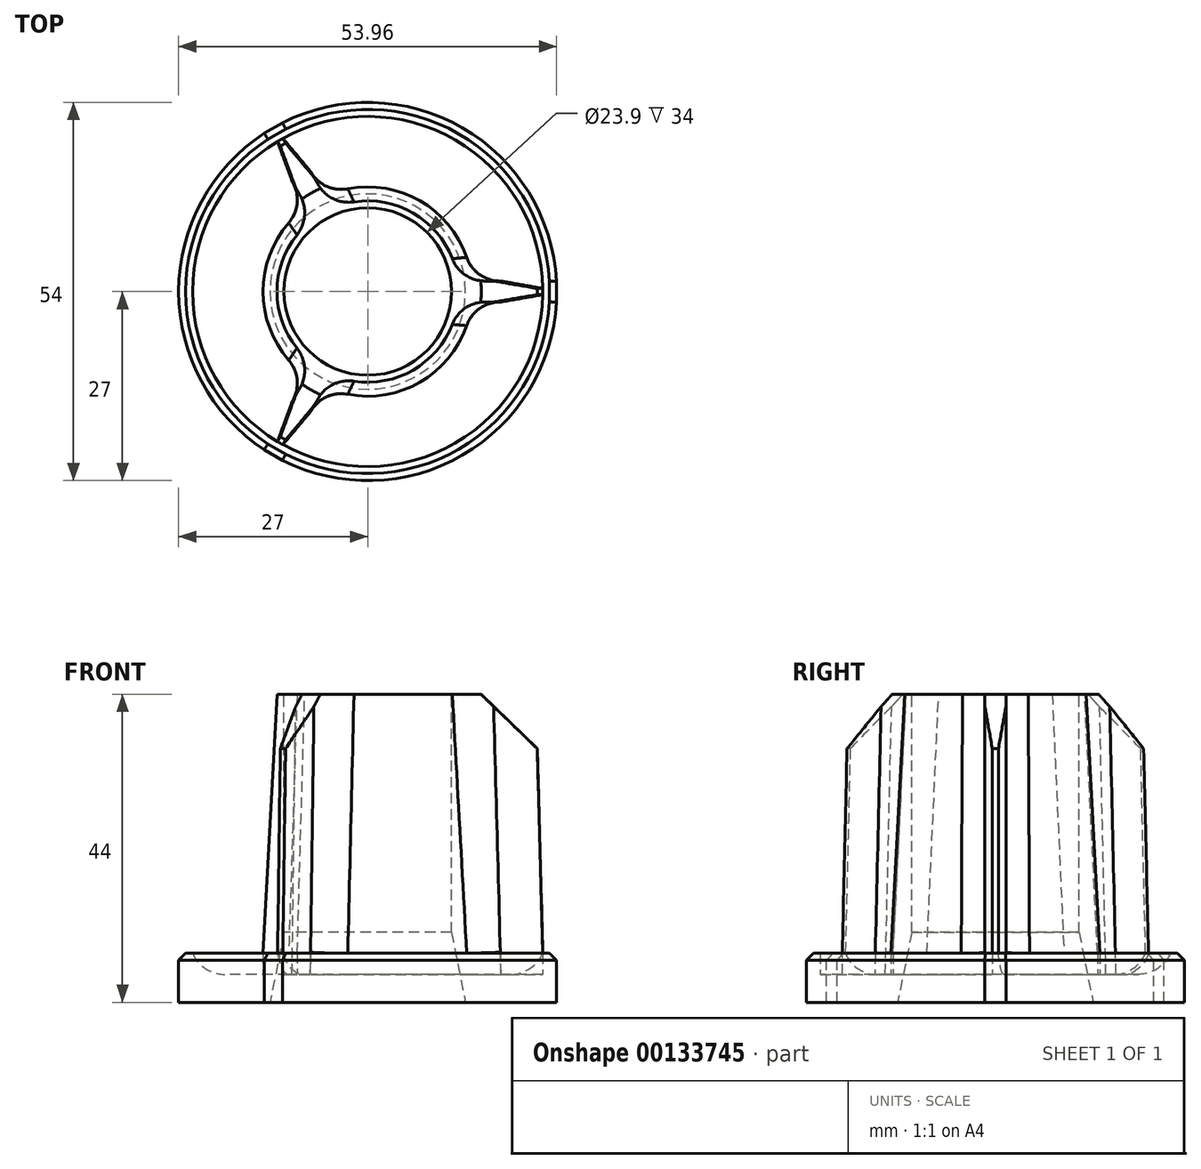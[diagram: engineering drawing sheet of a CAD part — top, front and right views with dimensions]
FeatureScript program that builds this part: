
annotation { "Feature Type Name" : "Feature", "Feature Type Description" : "" }
export const myFeature = defineFeature(function(context is Context, id is Id, definition is map)
    precondition{}
    {
        {
            var Q0;
            Q0=qCreatedBy(makeId("Top.planeOp"),FACE);
            var sketch = newSketch(context, id + "F0", { "sketchPlane" : qUnion([Q0])});
            skCircle(sketch, "E0", {"center": v(0, 0) * mm, "radius": 27 * mm});
            skCircle(sketch, "E1", {"center": v(0, 0) * mm, "radius": 11.95 * mm});
            skLineSegment(sketch, "E2", {"start": v(14.87, 1.5) * mm, "end": v(26.96, 1.5) * mm});
            skLineSegment(sketch, "E3", {"start": v(14.87, -1.5) * mm, "end": v(26.96, -1.5) * mm});
            skLineSegment(sketch, "E4", {"start": v(26.96, -1.5) * mm, "end": v(26.96, 1.5) * mm});
            skLineSegment(sketch, "E5.1.0", {"start": v(-6.14, 13.63) * mm, "end": v(-12.18, 24.1) * mm});
            skLineSegment(sketch, "E5.1.1", {"start": v(-12.18, 24.1) * mm, "end": v(-14.78, 22.6) * mm});
            skLineSegment(sketch, "E5.1.2", {"start": v(-8.74, 12.13) * mm, "end": v(-14.78, 22.6) * mm});
            skLineSegment(sketch, "E5.2.0", {"start": v(-8.74, -12.13) * mm, "end": v(-14.78, -22.6) * mm});
            skLineSegment(sketch, "E5.2.1", {"start": v(-14.78, -22.6) * mm, "end": v(-12.18, -24.1) * mm});
            skLineSegment(sketch, "E5.2.2", {"start": v(-6.14, -13.63) * mm, "end": v(-12.18, -24.1) * mm});
            skCircle(sketch, "E6", {"center": v(0, 0) * mm, "radius": 14.95 * mm, "construction": true});
            skArc(sketch, "E7", {"start": v(14.87, 1.5) * mm, "mid": v(7.47, 12.95) * mm, "end": v(-6.14, 13.63) * mm});
            skArc(sketch, "E8", {"start": v(-8.74, 12.13) * mm, "mid": v(-14.95, 0) * mm, "end": v(-8.74, -12.13) * mm});
            skArc(sketch, "E9", {"start": v(-6.14, -13.63) * mm, "mid": v(7.48, -12.95) * mm, "end": v(14.87, -1.5) * mm});
            skCircle(sketch, "E10", {"center": v(0, 0) * mm, "radius": 25 * mm});
            skSolve(sketch);
        }
        {
            var Q0;
            {var subQ0=sQuery(id+"F0.wireOp",EDGE,"E7");Q0=makeQuery(id+"F0.imprint","IMPRINT",FACE,{"disambiguationData":[TD([[makeQuery(id+"F0.imprint","IMPRINT",EDGE,{"derivedFrom":subQ0}),-1.0]])]});}
            var Q1;
            {var subQ0=sQuery(id+"F0.wireOp",EDGE,"E2");var subQ5=sQuery(id+"F0.wireOp",EDGE,"E10");var subQ6=makeQuery(id+"F0.imprint","INTERSECT",VERTEX,{"derivedFrom":[subQ0,subQ5]});Q1=makeQuery(id+"F0.imprint","IMPRINT",FACE,{"disambiguationData":[TD([[makeQuery(id+"F0.imprint","IMPRINT",EDGE,{"disambiguationData":[TD([[subQ6,-1.0]])],"derivedFrom":subQ5}),-1.0]])]});}
            var Q2;
            {var subQ0=sQuery(id+"F0.wireOp",EDGE,"E5.1.1");Q2=makeQuery(id+"F0.imprint","IMPRINT",FACE,{"disambiguationData":[TD([[makeQuery(id+"F0.imprint","IMPRINT",EDGE,{"derivedFrom":subQ0}),1.0]])]});}
            var Q3;
            {var subQ0=sQuery(id+"F0.wireOp",EDGE,"E5.1.2");var subQ5=sQuery(id+"F0.wireOp",EDGE,"E10");var subQ6=makeQuery(id+"F0.imprint","INTERSECT",VERTEX,{"derivedFrom":[subQ0,subQ5]});Q3=makeQuery(id+"F0.imprint","IMPRINT",FACE,{"disambiguationData":[TD([[makeQuery(id+"F0.imprint","IMPRINT",EDGE,{"disambiguationData":[TD([[subQ6,-1.0]])],"derivedFrom":subQ5}),-1.0]])]});}
            var Q4;
            {var subQ0=sQuery(id+"F0.wireOp",EDGE,"E9");Q4=makeQuery(id+"F0.imprint","IMPRINT",FACE,{"disambiguationData":[TD([[makeQuery(id+"F0.imprint","IMPRINT",EDGE,{"derivedFrom":subQ0}),-1.0]])]});}
            var Q5;
            {var subQ0=sQuery(id+"F0.wireOp",EDGE,"E3");var subQ5=sQuery(id+"F0.wireOp",EDGE,"E10");var subQ7=makeQuery(id+"F0.imprint","INTERSECT",VERTEX,{"derivedFrom":[subQ0,subQ5]});Q5=makeQuery(id+"F0.imprint","IMPRINT",FACE,{"disambiguationData":[TD([[makeQuery(id+"F0.imprint","IMPRINT",EDGE,{"disambiguationData":[TD([[subQ7,1.0]])],"derivedFrom":subQ5}),-1.0]])]});}
            var Q6;
            Q6=makeQuery(id+"F0.imprint","IMPRINT",FACE,{"disambiguationData":[TD([[makeQuery(id+"F0.imprint","IMPRINT",EDGE,{"derivedFrom":sQuery(id+"F0.wireOp",EDGE,"E1")}),-1.0]])]});
            var Q7;
            {var subQ0=sQuery(id+"F0.wireOp",EDGE,"E5.2.1");Q7=makeQuery(id+"F0.imprint","IMPRINT",FACE,{"disambiguationData":[TD([[makeQuery(id+"F0.imprint","IMPRINT",EDGE,{"derivedFrom":subQ0}),1.0]])]});}
            var Q8;
            {var subQ0=sQuery(id+"F0.wireOp",EDGE,"E4");Q8=makeQuery(id+"F0.imprint","IMPRINT",FACE,{"disambiguationData":[TD([[makeQuery(id+"F0.imprint","IMPRINT",EDGE,{"derivedFrom":subQ0}),1.0]])]});}
            var Q9;
            {var subQ0=sQuery(id+"F0.wireOp",EDGE,"E8");Q9=makeQuery(id+"F0.imprint","IMPRINT",FACE,{"disambiguationData":[TD([[makeQuery(id+"F0.imprint","IMPRINT",EDGE,{"derivedFrom":subQ0}),-1.0]])]});}
            extrude(context, id + "F1", {"entities" : qUnion([Q0, Q1, Q2, Q3, Q4, Q5, Q6, Q7, Q8, Q9]), "oppositeDirection" : true, "depth" : 4 * mm});
        }
        {
            var Q0;
            Q0=makeQuery(id+"F0.imprint","IMPRINT",FACE,{"disambiguationData":[TD([[makeQuery(id+"F0.imprint","IMPRINT",EDGE,{"derivedFrom":sQuery(id+"F0.wireOp",EDGE,"E1")}),-1.0]])]});
            extrude(context, id + "F2", {"entities" : qUnion([Q0]), "operationType" : NewBodyOperationType.ADD, "depth" : 40 * mm});
        }
        {
            var Q0;
            {var subQ0=sQuery(id+"F0.wireOp",EDGE,"E5.1.2");var subQ5=sQuery(id+"F0.wireOp",EDGE,"E10");var subQ6=makeQuery(id+"F0.imprint","INTERSECT",VERTEX,{"derivedFrom":[subQ0,subQ5]});Q0=makeQuery(id+"F0.imprint","IMPRINT",FACE,{"disambiguationData":[TD([[makeQuery(id+"F0.imprint","IMPRINT",EDGE,{"disambiguationData":[TD([[subQ6,-1.0]])],"derivedFrom":subQ5}),-1.0]])]});}
            var Q1;
            {var subQ0=sQuery(id+"F0.wireOp",EDGE,"E3");var subQ5=sQuery(id+"F0.wireOp",EDGE,"E10");var subQ7=makeQuery(id+"F0.imprint","INTERSECT",VERTEX,{"derivedFrom":[subQ0,subQ5]});Q1=makeQuery(id+"F0.imprint","IMPRINT",FACE,{"disambiguationData":[TD([[makeQuery(id+"F0.imprint","IMPRINT",EDGE,{"disambiguationData":[TD([[subQ7,1.0]])],"derivedFrom":subQ5}),-1.0]])]});}
            var Q2;
            {var subQ0=sQuery(id+"F0.wireOp",EDGE,"E5.2.1");Q2=makeQuery(id+"F0.imprint","IMPRINT",FACE,{"disambiguationData":[TD([[makeQuery(id+"F0.imprint","IMPRINT",EDGE,{"derivedFrom":subQ0}),1.0]])]});}
            var Q3;
            {var subQ0=sQuery(id+"F0.wireOp",EDGE,"E4");Q3=makeQuery(id+"F0.imprint","IMPRINT",FACE,{"disambiguationData":[TD([[makeQuery(id+"F0.imprint","IMPRINT",EDGE,{"derivedFrom":subQ0}),1.0]])]});}
            var Q4;
            {var subQ0=sQuery(id+"F0.wireOp",EDGE,"E2");var subQ5=sQuery(id+"F0.wireOp",EDGE,"E10");var subQ6=makeQuery(id+"F0.imprint","INTERSECT",VERTEX,{"derivedFrom":[subQ0,subQ5]});Q4=makeQuery(id+"F0.imprint","IMPRINT",FACE,{"disambiguationData":[TD([[makeQuery(id+"F0.imprint","IMPRINT",EDGE,{"disambiguationData":[TD([[subQ6,-1.0]])],"derivedFrom":subQ5}),-1.0]])]});}
            var Q5;
            {var subQ0=sQuery(id+"F0.wireOp",EDGE,"E5.1.1");Q5=makeQuery(id+"F0.imprint","IMPRINT",FACE,{"disambiguationData":[TD([[makeQuery(id+"F0.imprint","IMPRINT",EDGE,{"derivedFrom":subQ0}),1.0]])]});}
            extrude(context, id + "F3", {"entities" : qUnion([Q0, Q1, Q2, Q3, Q4, Q5]), "operationType" : NewBodyOperationType.ADD, "depth" : 3 * mm});
        }
        {
            var Q0;
            Q0=makeQuery(id+"F2.opExtrude","CAP_EDGE",EDGE,{"disambiguationData":[OSD([sQuery(id+"F0.wireOp",EDGE,"E7")])],"isStart":false});
            var Q1;
            Q1=makeQuery(id+"F2.opExtrude","CAP_EDGE",EDGE,{"disambiguationData":[OSD([sQuery(id+"F0.wireOp",EDGE,"E8")])],"isStart":false});
            var Q2;
            Q2=makeQuery(id+"F2.opExtrude","CAP_EDGE",EDGE,{"disambiguationData":[OSD([sQuery(id+"F0.wireOp",EDGE,"E9")])],"isStart":false});
            chamfer(context, id + "F4", {"entities" : qUnion([Q0, Q1, Q2]), "chamferType" : ChamferType.TWO_OFFSETS, "width1" : 2 * mm, "oppositeDirection" : false, "width2" : 37 * mm, "tangentPropagation" : true});
        }
        {
            var Q0;
            {var subQ0=sQuery(id+"F0.wireOp",EDGE,"E10");Q0=makeQuery(id+"F2.opExtrude","CAP_EDGE",EDGE,{"disambiguationData":[OSD([subQ0]),TDD([makeQuery(id+"F0.imprint","IMPRINT",EDGE,{"disambiguationData":[TD([[makeQuery(id+"F0.imprint","INTERSECT",VERTEX,{"derivedFrom":[sQuery(id+"F0.wireOp",EDGE,"E5.2.0"),subQ0]}),-1.0]])],"derivedFrom":subQ0})])],"isStart":false});}
            var Q1;
            {var subQ0=sQuery(id+"F0.wireOp",EDGE,"E10");Q1=makeQuery(id+"F2.opExtrude","CAP_EDGE",EDGE,{"disambiguationData":[OSD([subQ0]),TDD([makeQuery(id+"F0.imprint","IMPRINT",EDGE,{"disambiguationData":[TD([[makeQuery(id+"F0.imprint","INTERSECT",VERTEX,{"derivedFrom":[sQuery(id+"F0.wireOp",EDGE,"E2"),subQ0]}),1.0]])],"derivedFrom":subQ0})])],"isStart":false});}
            var Q2;
            {var subQ0=sQuery(id+"F0.wireOp",EDGE,"E10");Q2=makeQuery(id+"F2.opExtrude","CAP_EDGE",EDGE,{"disambiguationData":[OSD([subQ0]),TDD([makeQuery(id+"F0.imprint","IMPRINT",EDGE,{"disambiguationData":[TD([[makeQuery(id+"F0.imprint","INTERSECT",VERTEX,{"derivedFrom":[sQuery(id+"F0.wireOp",EDGE,"E5.1.0"),subQ0]}),-1.0]])],"derivedFrom":subQ0})])],"isStart":false});}
            chamfer(context, id + "F5", {"entities" : qUnion([Q0, Q1, Q2]), "chamferType" : ChamferType.TWO_OFFSETS, "width1" : 1 * mm, "oppositeDirection" : false, "width2" : 37 * mm, "tangentPropagation" : true});
        }
        {
            var Q0;
            Q0=makeQuery(id+"F1.opExtrude","CAP_EDGE",EDGE,{"disambiguationData":[OSD([sQuery(id+"F0.wireOp",EDGE,"E1")])],"isStart":false});
            chamfer(context, id + "F6", {"entities" : qUnion([Q0]), "chamferType" : ChamferType.TWO_OFFSETS, "width1" : 2 * mm, "oppositeDirection" : false, "width2" : 10 * mm, "tangentPropagation" : true});
        }
        {
            var Q0;
            Q0=makeQuery(id+"F4.opChamfer","BLEND_EDGE",EDGE,{"blendedFrom":[makeQuery(id+"F2.opExtrude","CAP_EDGE",EDGE,{"disambiguationData":[OSD([sQuery(id+"F0.wireOp",EDGE,"E7")])],"isStart":false}),makeQuery(id+"F2.opExtrude","SWEPT_FACE",FACE,{"disambiguationData":[OSD([sQuery(id+"F0.wireOp",EDGE,"E5.1.0")])]})],"blendedInto":[makeQuery(id+"F2.opExtrude","SWEPT_FACE",FACE,{"disambiguationData":[OSD([sQuery(id+"F0.wireOp",EDGE,"E5.1.0")])]})]});
            var Q1;
            Q1=makeQuery(id+"F4.opChamfer","BLEND_EDGE",EDGE,{"blendedFrom":[makeQuery(id+"F2.opExtrude","CAP_EDGE",EDGE,{"disambiguationData":[OSD([sQuery(id+"F0.wireOp",EDGE,"E7")])],"isStart":false}),makeQuery(id+"F2.opExtrude","SWEPT_FACE",FACE,{"disambiguationData":[OSD([sQuery(id+"F0.wireOp",EDGE,"E2")])]})],"blendedInto":[makeQuery(id+"F2.opExtrude","SWEPT_FACE",FACE,{"disambiguationData":[OSD([sQuery(id+"F0.wireOp",EDGE,"E2")])]})]});
            var Q2;
            Q2=makeQuery(id+"F4.opChamfer","BLEND_EDGE",EDGE,{"blendedFrom":[makeQuery(id+"F2.opExtrude","CAP_EDGE",EDGE,{"disambiguationData":[OSD([sQuery(id+"F0.wireOp",EDGE,"E9")])],"isStart":false}),makeQuery(id+"F2.opExtrude","SWEPT_FACE",FACE,{"disambiguationData":[OSD([sQuery(id+"F0.wireOp",EDGE,"E3")])]})],"blendedInto":[makeQuery(id+"F2.opExtrude","SWEPT_FACE",FACE,{"disambiguationData":[OSD([sQuery(id+"F0.wireOp",EDGE,"E3")])]})]});
            var Q3;
            Q3=makeQuery(id+"F4.opChamfer","BLEND_EDGE",EDGE,{"blendedFrom":[makeQuery(id+"F2.opExtrude","CAP_EDGE",EDGE,{"disambiguationData":[OSD([sQuery(id+"F0.wireOp",EDGE,"E9")])],"isStart":false}),makeQuery(id+"F2.opExtrude","SWEPT_FACE",FACE,{"disambiguationData":[OSD([sQuery(id+"F0.wireOp",EDGE,"E5.2.2")])]})],"blendedInto":[makeQuery(id+"F2.opExtrude","SWEPT_FACE",FACE,{"disambiguationData":[OSD([sQuery(id+"F0.wireOp",EDGE,"E5.2.2")])]})]});
            var Q4;
            Q4=makeQuery(id+"F4.opChamfer","BLEND_EDGE",EDGE,{"blendedFrom":[makeQuery(id+"F2.opExtrude","CAP_EDGE",EDGE,{"disambiguationData":[OSD([sQuery(id+"F0.wireOp",EDGE,"E8")])],"isStart":false}),makeQuery(id+"F2.opExtrude","SWEPT_FACE",FACE,{"disambiguationData":[OSD([sQuery(id+"F0.wireOp",EDGE,"E5.2.0")])]})],"blendedInto":[makeQuery(id+"F2.opExtrude","SWEPT_FACE",FACE,{"disambiguationData":[OSD([sQuery(id+"F0.wireOp",EDGE,"E5.2.0")])]})]});
            var Q5;
            Q5=makeQuery(id+"F4.opChamfer","BLEND_EDGE",EDGE,{"blendedFrom":[makeQuery(id+"F2.opExtrude","CAP_EDGE",EDGE,{"disambiguationData":[OSD([sQuery(id+"F0.wireOp",EDGE,"E8")])],"isStart":false}),makeQuery(id+"F2.opExtrude","SWEPT_FACE",FACE,{"disambiguationData":[OSD([sQuery(id+"F0.wireOp",EDGE,"E5.1.2")])]})],"blendedInto":[makeQuery(id+"F2.opExtrude","SWEPT_FACE",FACE,{"disambiguationData":[OSD([sQuery(id+"F0.wireOp",EDGE,"E5.1.2")])]})]});
            var Q6;
            Q6=makeQuery(id+"F2.opExtrude","CAP_EDGE",EDGE,{"disambiguationData":[OSD([sQuery(id+"F0.wireOp",EDGE,"E9")])],"isStart":true});
            var Q7;
            {var subQ0=sQuery(id+"F0.wireOp",EDGE,"E10");Q7=makeQuery(id+"F3.boolean.opBoolean","SPLIT",EDGE,{"disambiguationData":[TD([makeQuery(id+"F2.opExtrude","SWEPT_FACE",FACE,{"disambiguationData":[OSD([sQuery(id+"F0.wireOp",EDGE,"E3")])]})])],"derivedFrom":makeQuery(id+"F3.opExtrude","CAP_EDGE",EDGE,{"disambiguationData":[OSD([subQ0])],"isStart":true})});}
            var Q8;
            {var subQ0=sQuery(id+"F0.wireOp",EDGE,"E10");Q8=makeQuery(id+"F3.boolean.opBoolean","SPLIT",EDGE,{"disambiguationData":[TD([makeQuery(id+"F2.opExtrude","SWEPT_FACE",FACE,{"disambiguationData":[OSD([sQuery(id+"F0.wireOp",EDGE,"E5.1.2")])]})])],"derivedFrom":makeQuery(id+"F3.opExtrude","CAP_EDGE",EDGE,{"disambiguationData":[OSD([subQ0])],"isStart":true})});}
            var Q9;
            Q9=makeQuery(id+"F2.opExtrude","CAP_EDGE",EDGE,{"disambiguationData":[OSD([sQuery(id+"F0.wireOp",EDGE,"E8")])],"isStart":true});
            var Q10;
            Q10=makeQuery(id+"F2.opExtrude","CAP_EDGE",EDGE,{"disambiguationData":[OSD([sQuery(id+"F0.wireOp",EDGE,"E7")])],"isStart":true});
            var Q11;
            {var subQ0=sQuery(id+"F0.wireOp",EDGE,"E10");Q11=makeQuery(id+"F3.boolean.opBoolean","SPLIT",EDGE,{"disambiguationData":[TD([makeQuery(id+"F2.opExtrude","SWEPT_FACE",FACE,{"disambiguationData":[OSD([sQuery(id+"F0.wireOp",EDGE,"E2")])]})])],"derivedFrom":makeQuery(id+"F3.opExtrude","CAP_EDGE",EDGE,{"disambiguationData":[OSD([subQ0])],"isStart":true})});}
            fillet(context, id + "F7", {"entities" : qUnion([Q0, Q1, Q2, Q3, Q4, Q5, Q6, Q7, Q8, Q9, Q10, Q11]), "radius" : 5 * mm, "tangentPropagation" : true, "allowEdgeOverflow" : false});
        }
        {
            var Q0;
            {var subQ0=sQuery(id+"F0.wireOp",EDGE,"E10");var subQ1=sQuery(id+"F0.wireOp",EDGE,"E5.1.2");var subQ2=sQuery(id+"F0.wireOp",EDGE,"E5.1.0");Q0=makeQuery(id+"F5.opChamfer","BLEND_EDGE",EDGE,{"blendedFrom":[makeQuery(id+"F2.opExtrude","CAP_EDGE",EDGE,{"disambiguationData":[OSD([subQ0]),TDD([makeQuery(id+"F0.imprint","IMPRINT",EDGE,{"disambiguationData":[TD([[makeQuery(id+"F0.imprint","INTERSECT",VERTEX,{"derivedFrom":[subQ2,subQ0]}),-1.0]])],"derivedFrom":subQ0})])],"isStart":false}),makeQuery(id+"F2.opExtrude","CAP_FACE",FACE,{"disambiguationData":[OSD([sQuery(id+"F0.wireOp",EDGE,"E1"),sQuery(id+"F0.wireOp",EDGE,"E2"),sQuery(id+"F0.wireOp",EDGE,"E3"),subQ2,subQ1,sQuery(id+"F0.wireOp",EDGE,"E5.2.0"),sQuery(id+"F0.wireOp",EDGE,"E5.2.2"),sQuery(id+"F0.wireOp",EDGE,"E7"),sQuery(id+"F0.wireOp",EDGE,"E8"),sQuery(id+"F0.wireOp",EDGE,"E9"),subQ0])],"isStart":false})],"blendedInto":[makeQuery(id+"F2.opExtrude","CAP_FACE",FACE,{"disambiguationData":[OSD([sQuery(id+"F0.wireOp",EDGE,"E1"),sQuery(id+"F0.wireOp",EDGE,"E2"),sQuery(id+"F0.wireOp",EDGE,"E3"),subQ2,subQ1,sQuery(id+"F0.wireOp",EDGE,"E5.2.0"),sQuery(id+"F0.wireOp",EDGE,"E5.2.2"),sQuery(id+"F0.wireOp",EDGE,"E7"),sQuery(id+"F0.wireOp",EDGE,"E8"),sQuery(id+"F0.wireOp",EDGE,"E9"),subQ0])],"isStart":false})]});}
            var Q1;
            {var subQ0=sQuery(id+"F0.wireOp",EDGE,"E10");var subQ1=sQuery(id+"F0.wireOp",EDGE,"E3");var subQ2=sQuery(id+"F0.wireOp",EDGE,"E2");Q1=makeQuery(id+"F5.opChamfer","BLEND_EDGE",EDGE,{"blendedFrom":[makeQuery(id+"F2.opExtrude","CAP_EDGE",EDGE,{"disambiguationData":[OSD([subQ0]),TDD([makeQuery(id+"F0.imprint","IMPRINT",EDGE,{"disambiguationData":[TD([[makeQuery(id+"F0.imprint","INTERSECT",VERTEX,{"derivedFrom":[subQ2,subQ0]}),1.0]])],"derivedFrom":subQ0})])],"isStart":false}),makeQuery(id+"F2.opExtrude","CAP_FACE",FACE,{"disambiguationData":[OSD([sQuery(id+"F0.wireOp",EDGE,"E1"),subQ2,subQ1,sQuery(id+"F0.wireOp",EDGE,"E5.1.0"),sQuery(id+"F0.wireOp",EDGE,"E5.1.2"),sQuery(id+"F0.wireOp",EDGE,"E5.2.0"),sQuery(id+"F0.wireOp",EDGE,"E5.2.2"),sQuery(id+"F0.wireOp",EDGE,"E7"),sQuery(id+"F0.wireOp",EDGE,"E8"),sQuery(id+"F0.wireOp",EDGE,"E9"),subQ0])],"isStart":false})],"blendedInto":[makeQuery(id+"F2.opExtrude","CAP_FACE",FACE,{"disambiguationData":[OSD([sQuery(id+"F0.wireOp",EDGE,"E1"),subQ2,subQ1,sQuery(id+"F0.wireOp",EDGE,"E5.1.0"),sQuery(id+"F0.wireOp",EDGE,"E5.1.2"),sQuery(id+"F0.wireOp",EDGE,"E5.2.0"),sQuery(id+"F0.wireOp",EDGE,"E5.2.2"),sQuery(id+"F0.wireOp",EDGE,"E7"),sQuery(id+"F0.wireOp",EDGE,"E8"),sQuery(id+"F0.wireOp",EDGE,"E9"),subQ0])],"isStart":false})]});}
            var Q2;
            {var subQ0=sQuery(id+"F0.wireOp",EDGE,"E10");var subQ1=sQuery(id+"F0.wireOp",EDGE,"E5.2.2");var subQ2=sQuery(id+"F0.wireOp",EDGE,"E5.2.0");Q2=makeQuery(id+"F5.opChamfer","BLEND_EDGE",EDGE,{"blendedFrom":[makeQuery(id+"F2.opExtrude","CAP_EDGE",EDGE,{"disambiguationData":[OSD([subQ0]),TDD([makeQuery(id+"F0.imprint","IMPRINT",EDGE,{"disambiguationData":[TD([[makeQuery(id+"F0.imprint","INTERSECT",VERTEX,{"derivedFrom":[subQ2,subQ0]}),-1.0]])],"derivedFrom":subQ0})])],"isStart":false}),makeQuery(id+"F2.opExtrude","CAP_FACE",FACE,{"disambiguationData":[OSD([sQuery(id+"F0.wireOp",EDGE,"E1"),sQuery(id+"F0.wireOp",EDGE,"E2"),sQuery(id+"F0.wireOp",EDGE,"E3"),sQuery(id+"F0.wireOp",EDGE,"E5.1.0"),sQuery(id+"F0.wireOp",EDGE,"E5.1.2"),subQ2,subQ1,sQuery(id+"F0.wireOp",EDGE,"E7"),sQuery(id+"F0.wireOp",EDGE,"E8"),sQuery(id+"F0.wireOp",EDGE,"E9"),subQ0])],"isStart":false})],"blendedInto":[makeQuery(id+"F2.opExtrude","CAP_FACE",FACE,{"disambiguationData":[OSD([sQuery(id+"F0.wireOp",EDGE,"E1"),sQuery(id+"F0.wireOp",EDGE,"E2"),sQuery(id+"F0.wireOp",EDGE,"E3"),sQuery(id+"F0.wireOp",EDGE,"E5.1.0"),sQuery(id+"F0.wireOp",EDGE,"E5.1.2"),subQ2,subQ1,sQuery(id+"F0.wireOp",EDGE,"E7"),sQuery(id+"F0.wireOp",EDGE,"E8"),sQuery(id+"F0.wireOp",EDGE,"E9"),subQ0])],"isStart":false})]});}
            chamfer(context, id + "F8", {"entities" : qUnion([Q0, Q1, Q2]), "width" : 8 * mm, "tangentPropagation" : true});
        }
        {
            var Q0;
            {var subQ0=sQuery(id+"F0.wireOp",EDGE,"E5.1.2");var subQ1=sQuery(id+"F0.wireOp",EDGE,"E10");Q0=makeQuery(id+"F5.opChamfer","BLEND_EDGE",EDGE,{"blendedFrom":[makeQuery(id+"F2.opExtrude","CAP_EDGE",EDGE,{"disambiguationData":[OSD([subQ1]),TDD([makeQuery(id+"F0.imprint","IMPRINT",EDGE,{"disambiguationData":[TD([[makeQuery(id+"F0.imprint","INTERSECT",VERTEX,{"derivedFrom":[sQuery(id+"F0.wireOp",EDGE,"E5.1.0"),subQ1]}),-1.0]])],"derivedFrom":subQ1})])],"isStart":false}),makeQuery(id+"F2.opExtrude","SWEPT_FACE",FACE,{"disambiguationData":[OSD([subQ0])]})],"blendedInto":[makeQuery(id+"F2.opExtrude","SWEPT_FACE",FACE,{"disambiguationData":[OSD([subQ0])]})]});}
            var Q1;
            {var subQ0=sQuery(id+"F0.wireOp",EDGE,"E5.2.0");var subQ1=sQuery(id+"F0.wireOp",EDGE,"E10");Q1=makeQuery(id+"F5.opChamfer","BLEND_EDGE",EDGE,{"blendedFrom":[makeQuery(id+"F2.opExtrude","CAP_EDGE",EDGE,{"disambiguationData":[OSD([subQ1]),TDD([makeQuery(id+"F0.imprint","IMPRINT",EDGE,{"disambiguationData":[TD([[makeQuery(id+"F0.imprint","INTERSECT",VERTEX,{"derivedFrom":[subQ0,subQ1]}),-1.0]])],"derivedFrom":subQ1})])],"isStart":false}),makeQuery(id+"F2.opExtrude","SWEPT_FACE",FACE,{"disambiguationData":[OSD([subQ0])]})],"blendedInto":[makeQuery(id+"F2.opExtrude","SWEPT_FACE",FACE,{"disambiguationData":[OSD([subQ0])]})]});}
            var Q2;
            {var subQ0=sQuery(id+"F0.wireOp",EDGE,"E5.2.2");var subQ1=sQuery(id+"F0.wireOp",EDGE,"E10");Q2=makeQuery(id+"F5.opChamfer","BLEND_EDGE",EDGE,{"blendedFrom":[makeQuery(id+"F2.opExtrude","CAP_EDGE",EDGE,{"disambiguationData":[OSD([subQ1]),TDD([makeQuery(id+"F0.imprint","IMPRINT",EDGE,{"disambiguationData":[TD([[makeQuery(id+"F0.imprint","INTERSECT",VERTEX,{"derivedFrom":[sQuery(id+"F0.wireOp",EDGE,"E5.2.0"),subQ1]}),-1.0]])],"derivedFrom":subQ1})])],"isStart":false}),makeQuery(id+"F2.opExtrude","SWEPT_FACE",FACE,{"disambiguationData":[OSD([subQ0])]})],"blendedInto":[makeQuery(id+"F2.opExtrude","SWEPT_FACE",FACE,{"disambiguationData":[OSD([subQ0])]})]});}
            var Q3;
            {var subQ0=sQuery(id+"F0.wireOp",EDGE,"E5.1.0");var subQ1=sQuery(id+"F0.wireOp",EDGE,"E10");Q3=makeQuery(id+"F5.opChamfer","BLEND_EDGE",EDGE,{"blendedFrom":[makeQuery(id+"F2.opExtrude","CAP_EDGE",EDGE,{"disambiguationData":[OSD([subQ1]),TDD([makeQuery(id+"F0.imprint","IMPRINT",EDGE,{"disambiguationData":[TD([[makeQuery(id+"F0.imprint","INTERSECT",VERTEX,{"derivedFrom":[subQ0,subQ1]}),-1.0]])],"derivedFrom":subQ1})])],"isStart":false}),makeQuery(id+"F2.opExtrude","SWEPT_FACE",FACE,{"disambiguationData":[OSD([subQ0])]})],"blendedInto":[makeQuery(id+"F2.opExtrude","SWEPT_FACE",FACE,{"disambiguationData":[OSD([subQ0])]})]});}
            var Q4;
            {var subQ0=sQuery(id+"F0.wireOp",EDGE,"E2");var subQ1=sQuery(id+"F0.wireOp",EDGE,"E10");Q4=makeQuery(id+"F5.opChamfer","BLEND_EDGE",EDGE,{"blendedFrom":[makeQuery(id+"F2.opExtrude","CAP_EDGE",EDGE,{"disambiguationData":[OSD([subQ1]),TDD([makeQuery(id+"F0.imprint","IMPRINT",EDGE,{"disambiguationData":[TD([[makeQuery(id+"F0.imprint","INTERSECT",VERTEX,{"derivedFrom":[subQ0,subQ1]}),1.0]])],"derivedFrom":subQ1})])],"isStart":false}),makeQuery(id+"F2.opExtrude","SWEPT_FACE",FACE,{"disambiguationData":[OSD([subQ0])]})],"blendedInto":[makeQuery(id+"F2.opExtrude","SWEPT_FACE",FACE,{"disambiguationData":[OSD([subQ0])]})]});}
            var Q5;
            {var subQ0=sQuery(id+"F0.wireOp",EDGE,"E3");var subQ1=sQuery(id+"F0.wireOp",EDGE,"E10");Q5=makeQuery(id+"F5.opChamfer","BLEND_EDGE",EDGE,{"blendedFrom":[makeQuery(id+"F2.opExtrude","CAP_EDGE",EDGE,{"disambiguationData":[OSD([subQ1]),TDD([makeQuery(id+"F0.imprint","IMPRINT",EDGE,{"disambiguationData":[TD([[makeQuery(id+"F0.imprint","INTERSECT",VERTEX,{"derivedFrom":[sQuery(id+"F0.wireOp",EDGE,"E2"),subQ1]}),1.0]])],"derivedFrom":subQ1})])],"isStart":false}),makeQuery(id+"F2.opExtrude","SWEPT_FACE",FACE,{"disambiguationData":[OSD([subQ0])]})],"blendedInto":[makeQuery(id+"F2.opExtrude","SWEPT_FACE",FACE,{"disambiguationData":[OSD([subQ0])]})]});}
            chamfer(context, id + "F9", {"entities" : qUnion([Q0, Q1, Q2, Q3, Q4, Q5]), "chamferType" : ChamferType.TWO_OFFSETS, "width1" : 6 * mm, "oppositeDirection" : false, "width2" : 0.8 * mm, "tangentPropagation" : true});
        }
        {
            var Q0;
            {var subQ0=sQuery(id+"F0.wireOp",EDGE,"E0");Q0=makeQuery(id+"F3.opExtrude","CAP_EDGE",EDGE,{"disambiguationData":[OSD([subQ0]),TDD([makeQuery(id+"F0.imprint","IMPRINT",EDGE,{"disambiguationData":[TD([[makeQuery(id+"F0.imprint","INTERSECT",VERTEX,{"derivedFrom":[subQ0,sQuery(id+"F0.wireOp",EDGE,"E2"),sQuery(id+"F0.wireOp",EDGE,"E4")]}),-1.0]])],"derivedFrom":subQ0})])],"isStart":false});}
            var Q1;
            Q1=makeQuery(id+"F3.opExtrude","CAP_EDGE",EDGE,{"disambiguationData":[OSD([sQuery(id+"F0.wireOp",EDGE,"E5.1.1")])],"isStart":false});
            var Q2;
            {var subQ0=sQuery(id+"F0.wireOp",EDGE,"E0");Q2=makeQuery(id+"F3.opExtrude","CAP_EDGE",EDGE,{"disambiguationData":[OSD([subQ0]),TDD([makeQuery(id+"F0.imprint","IMPRINT",EDGE,{"disambiguationData":[TD([[makeQuery(id+"F0.imprint","INTERSECT",VERTEX,{"derivedFrom":[subQ0,sQuery(id+"F0.wireOp",EDGE,"E5.1.1"),sQuery(id+"F0.wireOp",EDGE,"E5.1.2")]}),-1.0]])],"derivedFrom":subQ0})])],"isStart":false});}
            var Q3;
            Q3=makeQuery(id+"F3.opExtrude","CAP_EDGE",EDGE,{"disambiguationData":[OSD([sQuery(id+"F0.wireOp",EDGE,"E5.2.1")])],"isStart":false});
            var Q4;
            {var subQ0=sQuery(id+"F0.wireOp",EDGE,"E0");Q4=makeQuery(id+"F3.opExtrude","CAP_EDGE",EDGE,{"disambiguationData":[OSD([subQ0]),TDD([makeQuery(id+"F0.imprint","IMPRINT",EDGE,{"disambiguationData":[TD([[makeQuery(id+"F0.imprint","INTERSECT",VERTEX,{"derivedFrom":[subQ0,sQuery(id+"F0.wireOp",EDGE,"E3"),sQuery(id+"F0.wireOp",EDGE,"E4")]}),1.0]])],"derivedFrom":subQ0})])],"isStart":false});}
            var Q5;
            Q5=makeQuery(id+"F3.opExtrude","CAP_EDGE",EDGE,{"disambiguationData":[OSD([sQuery(id+"F0.wireOp",EDGE,"E4")])],"isStart":false});
            chamfer(context, id + "F10", {"entities" : qUnion([Q0, Q1, Q2, Q3, Q4, Q5]), "width" : 1 * mm, "tangentPropagation" : true});
        }
    });
